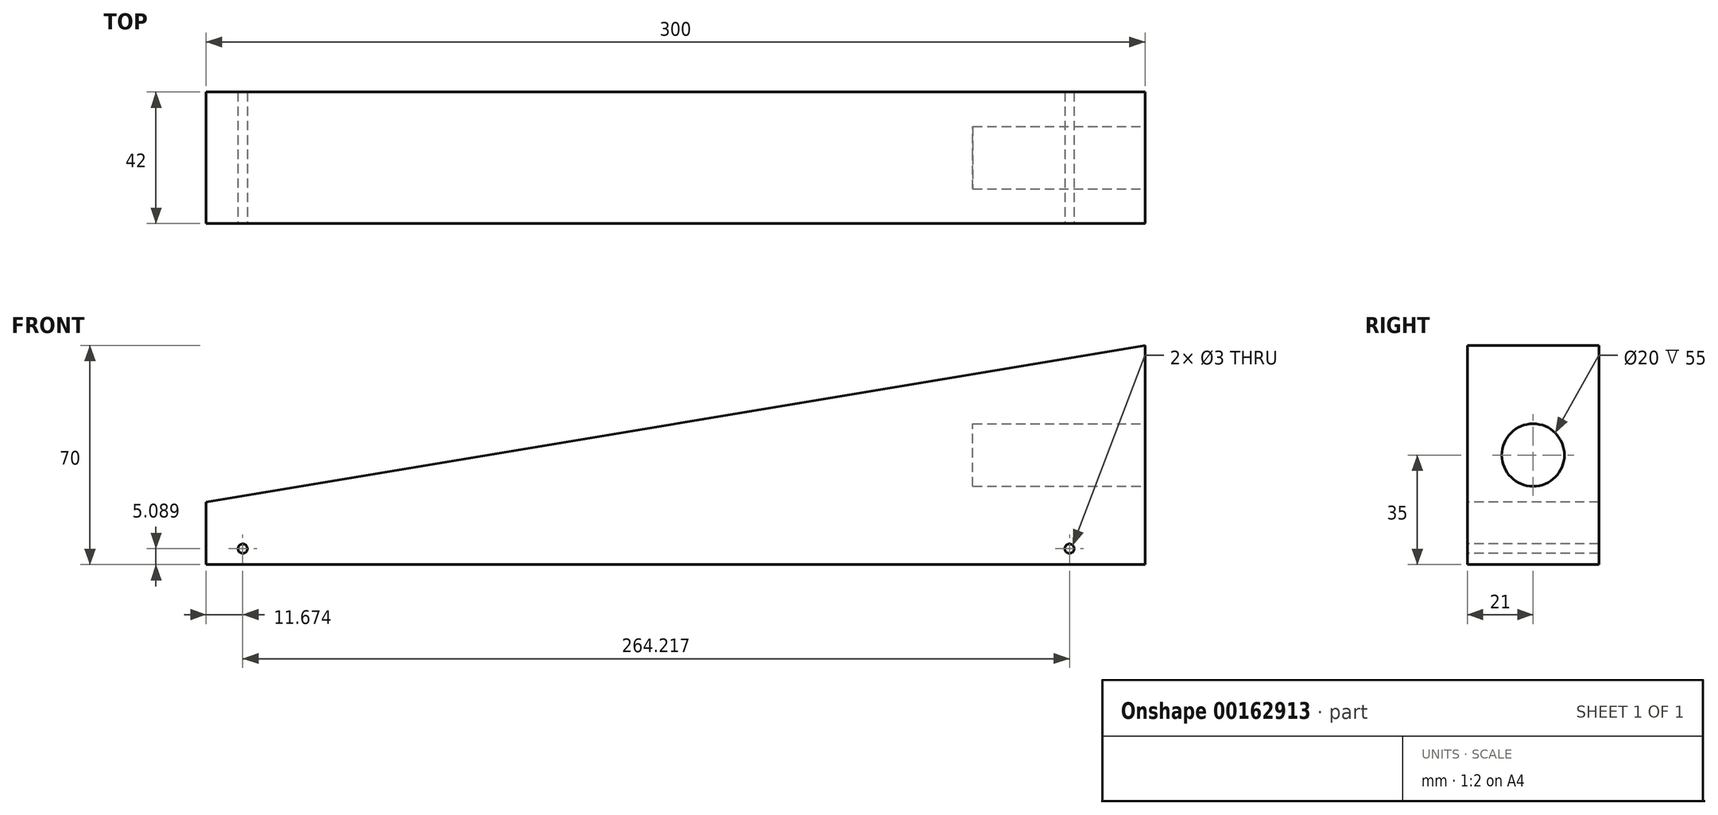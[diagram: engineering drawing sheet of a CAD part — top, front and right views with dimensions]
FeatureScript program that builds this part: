
annotation { "Feature Type Name" : "Feature", "Feature Type Description" : "" }
export const myFeature = defineFeature(function(context is Context, id is Id, definition is map)
    precondition{}
    {
        {
            var Q0;
            Q0=qCreatedBy(makeId("Front.planeOp"),FACE);
            var sketch = newSketch(context, id + "F0", { "sketchPlane" : qUnion([Q0])});
            skLineSegment(sketch, "E0", {"start": v(172.6, 0) * mm, "end": v(-127.4, 0) * mm});
            skLineSegment(sketch, "E1", {"start": v(172.6, 0) * mm, "end": v(172.6, 70) * mm});
            skLineSegment(sketch, "E2", {"start": v(172.6, 70) * mm, "end": v(-127.4, 20) * mm});
            skLineSegment(sketch, "E3", {"start": v(-127.4, 20) * mm, "end": v(-127.4, 0) * mm});
            skSolve(sketch);
        }
        {
            var Q0;
            Q0=makeQuery(id+"F0.imprint","IMPRINT",FACE,{"disambiguationData":[TD([[makeQuery(id+"F0.imprint","IMPRINT",EDGE,{"derivedFrom":sQuery(id+"F0.wireOp",EDGE,"E0")}),-1.0]])]});
            extrude(context, id + "F1", {"entities" : qUnion([Q0]), "oppositeDirection" : true, "depth" : 42 * mm});
        }
        {
            var Q0;
            Q0=makeQuery(id+"F1.opExtrude","SWEPT_FACE",FACE,{"disambiguationData":[OSD([sQuery(id+"F0.wireOp",EDGE,"E1")])]});
            var sketch = newSketch(context, id + "F2", { "sketchPlane" : qUnion([Q0])});
            skCircle(sketch, "E4", {"center": v(21, 35) * mm, "radius": 10 * mm});
            skSolve(sketch);
        }
        {
            var Q0;
            Q0 = qSketchRegion(id + "F2", true);
            extrude(context, id + "F3", {"entities" : qUnion([Q0]), "operationType" : NewBodyOperationType.REMOVE, "oppositeDirection" : true, "depth" : 55 * mm});
        }
        {
            var Q0;
            Q0=makeQuery(id+"F1.opExtrude","CAP_FACE",FACE,{"disambiguationData":[OSD([sQuery(id+"F0.wireOp",EDGE,"E0"),sQuery(id+"F0.wireOp",EDGE,"E1"),sQuery(id+"F0.wireOp",EDGE,"E2"),sQuery(id+"F0.wireOp",EDGE,"E3")])],"isStart":true});
            var sketch = newSketch(context, id + "F4", { "sketchPlane" : qUnion([Q0])});
            skCircle(sketch, "E5", {"center": v(-115.74, 5.09) * mm, "radius": 1.5 * mm});
            skCircle(sketch, "E6", {"center": v(148.48, 5.09) * mm, "radius": 1.5 * mm});
            skSolve(sketch);
        }
        {
            var Q0;
            Q0 = qSketchRegion(id + "F4", true);
            extrude(context, id + "F5", {"entities" : qUnion([Q0]), "operationType" : NewBodyOperationType.REMOVE, "oppositeDirection" : true, "depth" : 197.5 * mm});
        }
    });
